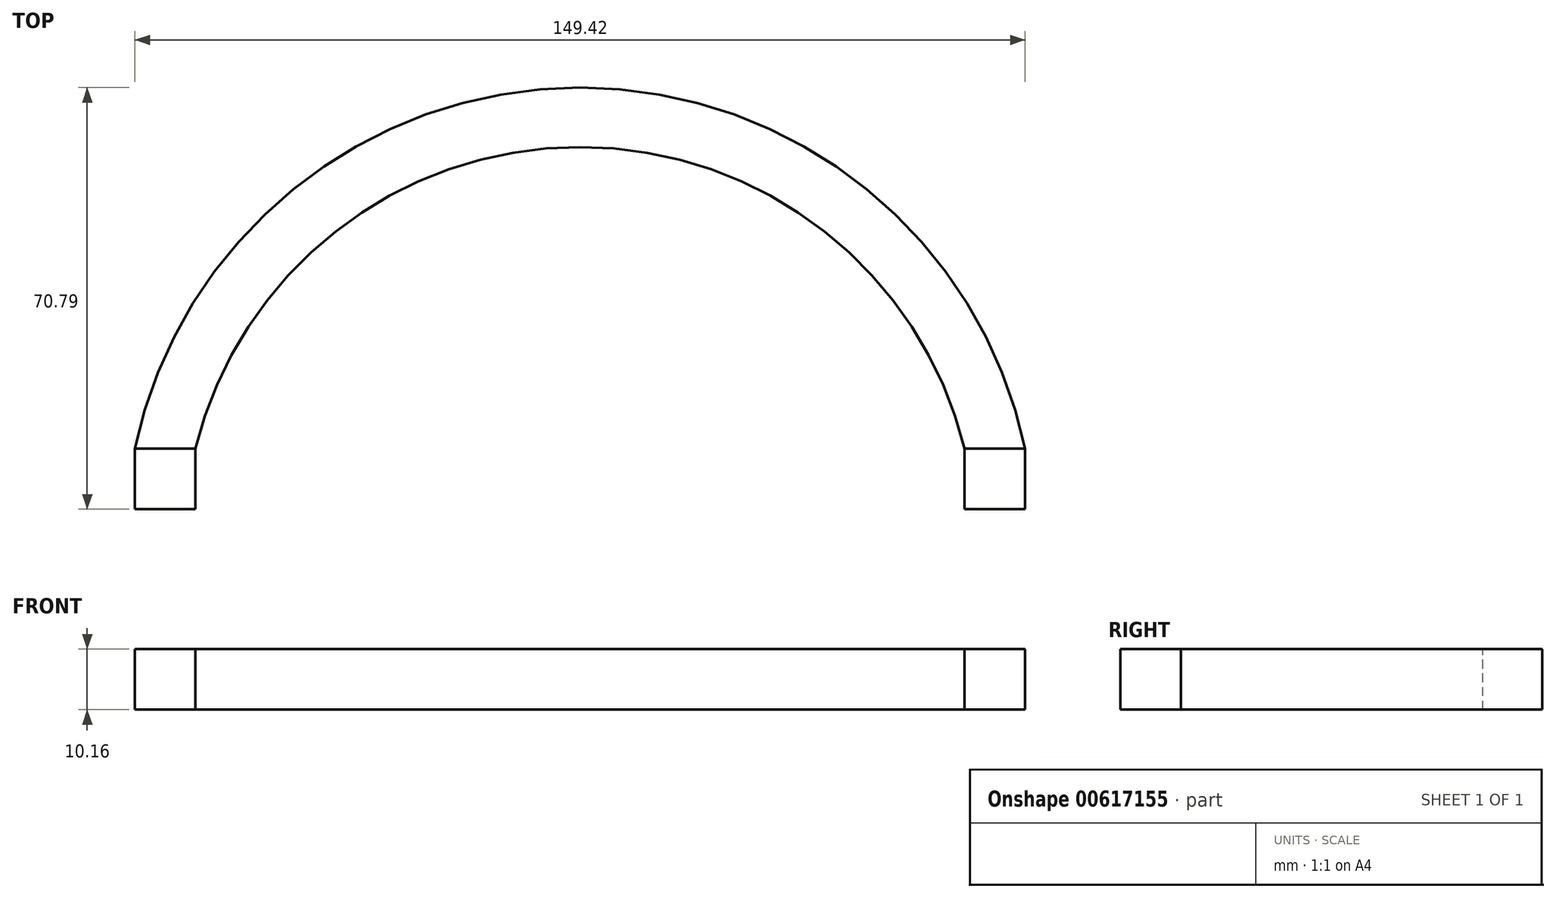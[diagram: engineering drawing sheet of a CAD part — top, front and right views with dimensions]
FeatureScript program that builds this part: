
annotation { "Feature Type Name" : "Feature", "Feature Type Description" : "" }
export const myFeature = defineFeature(function(context is Context, id is Id, definition is map)
    precondition{}
    {
        {
            var Q0;
            Q0=qCreatedBy(makeId("Front.planeOp"),FACE);
            var sketch = newSketch(context, id + "F0", { "sketchPlane" : qUnion([Q0])});
            skLineSegment(sketch, "E0.bottom", {"start": v(-108.2, -35.03) * mm, "end": v(-98.03, -35.03) * mm});
            skLineSegment(sketch, "E0.top", {"start": v(-108.2, -24.87) * mm, "end": v(-98.03, -24.87) * mm});
            skLineSegment(sketch, "E0.left", {"start": v(-108.2, -35.03) * mm, "end": v(-108.2, -24.87) * mm});
            skLineSegment(sketch, "E0.right", {"start": v(-98.03, -35.03) * mm, "end": v(-98.03, -24.87) * mm});
            skLineSegment(sketch, "E1.bottom", {"start": v(31.07, -35.03) * mm, "end": v(41.23, -35.03) * mm});
            skLineSegment(sketch, "E1.top", {"start": v(31.07, -24.87) * mm, "end": v(41.23, -24.87) * mm});
            skLineSegment(sketch, "E1.left", {"start": v(31.07, -35.03) * mm, "end": v(31.07, -24.87) * mm});
            skLineSegment(sketch, "E1.right", {"start": v(41.23, -35.03) * mm, "end": v(41.23, -24.87) * mm});
            skLineSegment(sketch, "E2", {"start": v(-103.11, -24.87) * mm, "end": v(-103.11, -29.95) * mm});
            skPoint(sketch, "E2.endSnap0", {"position": v(-108.2, -29.95) * mm});
            skLineSegment(sketch, "E3", {"start": v(36.15, -24.87) * mm, "end": v(36.15, -29.95) * mm});
            skPoint(sketch, "E3.endSnap0", {"position": v(41.23, -29.95) * mm});
            skSolve(sketch);
        }
        {
            var Q0;
            Q0 = qSketchRegion(id + "F0", true);
            extrude(context, id + "F1", {"entities" : qUnion([Q0]), "oppositeDirection" : true, "depth" : 10.16 * mm, "offsetDistance" : 25.4 * mm});
        }
        {
            var Q0;
            Q0=makeQuery(id+"F1.opExtrude","SWEPT_FACE",FACE,{"disambiguationData":[OSD([sQuery(id+"F0.wireOp",EDGE,"E0.top")])]});
            var sketch = newSketch(context, id + "F2", { "sketchPlane" : qUnion([Q0])});
            skLineSegment(sketch, "E4.0.2", {"start": v(-98.03, 10.16) * mm, "end": v(-108.2, 10.16) * mm});
            skLineSegment(sketch, "E5.0.2", {"start": v(41.23, 10.16) * mm, "end": v(31.07, 10.16) * mm});
            skArc(sketch, "E6", {"start": v(31.07, 10.16) * mm, "mid": v(-33.48, 60.81) * mm, "end": v(-98.03, 10.16) * mm});
            skArc(sketch, "E7", {"start": v(41.23, 10.16) * mm, "mid": v(-33.48, 70.8) * mm, "end": v(-108.2, 10.16) * mm});
            skSolve(sketch);
        }
        {
            var Q0;
            Q0 = qSketchRegion(id + "F2", true);
            extrude(context, id + "F3", {"entities" : qUnion([Q0]), "oppositeDirection" : true, "depth" : 10.16 * mm, "offsetDistance" : 25.4 * mm});
        }
    });
